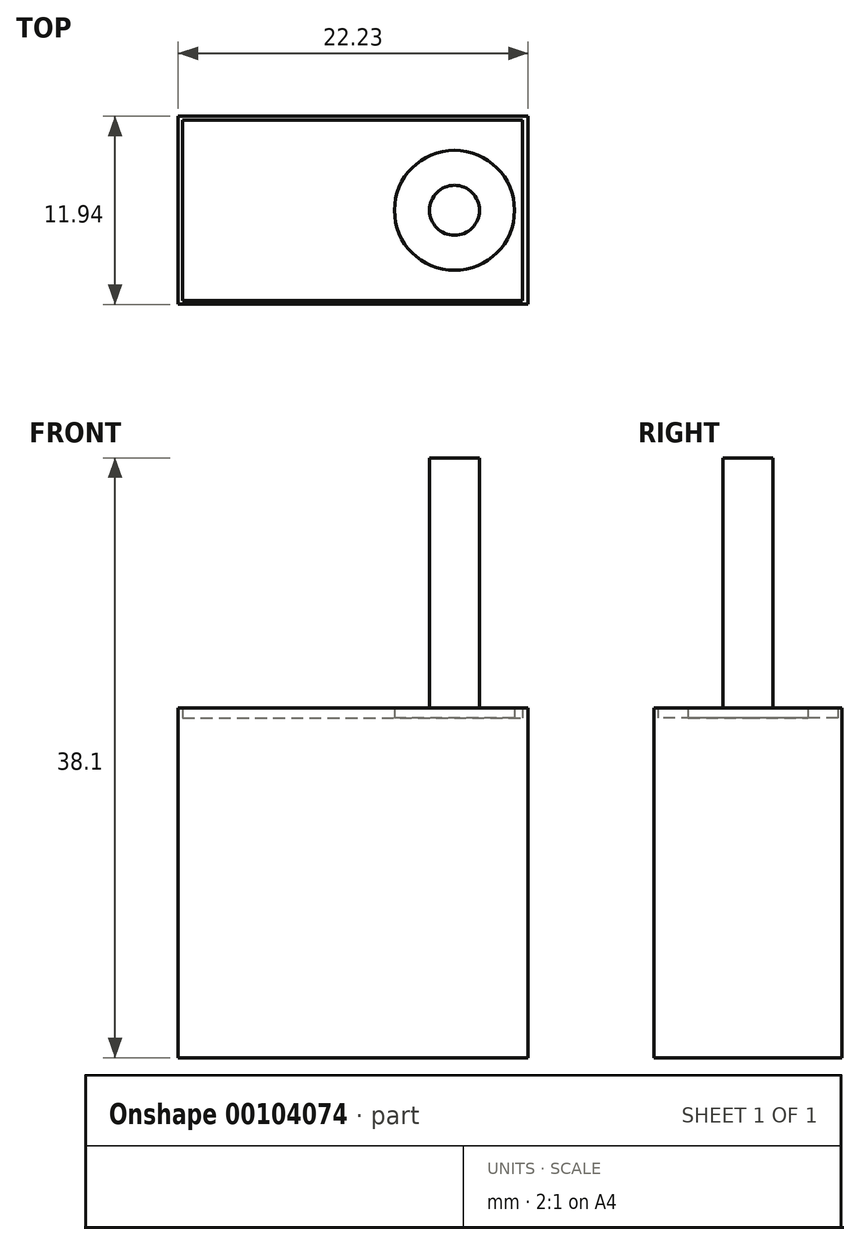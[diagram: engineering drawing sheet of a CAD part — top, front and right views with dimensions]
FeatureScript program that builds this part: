
annotation { "Feature Type Name" : "Feature", "Feature Type Description" : "" }
export const myFeature = defineFeature(function(context is Context, id is Id, definition is map)
    precondition{}
    {
        {
            var Q0;
            Q0=qCreatedBy(makeId("Top.planeOp"),FACE);
            var sketch = newSketch(context, id + "F0", { "sketchPlane" : qUnion([Q0])});
            skLineSegment(sketch, "E0.bottom", {"start": v(-55.63, 21.9) * mm, "end": v(-33.4, 21.9) * mm});
            skLineSegment(sketch, "E0.top", {"start": v(-55.63, 9.97) * mm, "end": v(-33.4, 9.97) * mm});
            skLineSegment(sketch, "E0.left", {"start": v(-55.63, 21.9) * mm, "end": v(-55.63, 9.97) * mm});
            skLineSegment(sketch, "E0.right", {"start": v(-33.4, 21.9) * mm, "end": v(-33.4, 9.97) * mm});
            skCircle(sketch, "E1", {"center": v(-38.08, 15.94) * mm, "radius": 3.81 * mm});
            skPoint(sketch, "E1.centerSnap0", {"position": v(-33.4, 15.94) * mm});
            skCircle(sketch, "E2", {"center": v(-38.08, 15.94) * mm, "radius": 1.59 * mm});
            skLineSegment(sketch, "E3.bottom", {"start": v(-55.34, 21.66) * mm, "end": v(-33.75, 21.66) * mm});
            skLineSegment(sketch, "E3.top", {"start": v(-55.34, 10.22) * mm, "end": v(-33.75, 10.22) * mm});
            skLineSegment(sketch, "E3.left", {"start": v(-55.34, 21.66) * mm, "end": v(-55.34, 10.22) * mm});
            skLineSegment(sketch, "E3.right", {"start": v(-33.75, 21.66) * mm, "end": v(-33.75, 10.22) * mm});
            skPoint(sketch, "E4", {"position": v(-44.52, 21.9) * mm});
            skPoint(sketch, "E5", {"position": v(-44.52, 15.94) * mm});
            skPoint(sketch, "E6", {"position": v(-44.52, 9.97) * mm});
            skSolve(sketch);
        }
        {
            var Q0;
            Q0=makeQuery(id+"F0.imprint","IMPRINT",FACE,{"disambiguationData":[TD([[makeQuery(id+"F0.imprint","IMPRINT",EDGE,{"derivedFrom":sQuery(id+"F0.wireOp",EDGE,"E0.bottom")}),-1.0]])]});
            extrude(context, id + "F1", {"entities" : qUnion([Q0]), "depth" : 22.22 * mm});
        }
        {
            var Q0;
            Q0=makeQuery(id+"F0.imprint","IMPRINT",FACE,{"disambiguationData":[TD([[makeQuery(id+"F0.imprint","IMPRINT",EDGE,{"derivedFrom":sQuery(id+"F0.wireOp",EDGE,"E1")}),1.0]])]});
            extrude(context, id + "F2", {"entities" : qUnion([Q0]), "operationType" : NewBodyOperationType.ADD, "depth" : 22.22 * mm});
        }
        {
            var Q0;
            Q0=makeQuery(id+"F0.imprint","IMPRINT",FACE,{"disambiguationData":[TD([[makeQuery(id+"F0.imprint","IMPRINT",EDGE,{"derivedFrom":sQuery(id+"F0.wireOp",EDGE,"E2")}),1.0]])]});
            extrude(context, id + "F3", {"entities" : qUnion([Q0]), "operationType" : NewBodyOperationType.ADD, "depth" : 38.1 * mm});
        }
        {
            var Q0;
            Q0=makeQuery(id+"F0.imprint","IMPRINT",FACE,{"disambiguationData":[TD([[makeQuery(id+"F0.imprint","IMPRINT",EDGE,{"derivedFrom":sQuery(id+"F0.wireOp",EDGE,"E1")}),-1.0]])]});
            var Q1;
            Q1=makeQuery(id+"F0.imprint","IMPRINT",FACE,{"disambiguationData":[TD([[makeQuery(id+"F0.imprint","IMPRINT",EDGE,{"derivedFrom":sQuery(id+"F0.wireOp",EDGE,"E0.bottom")}),-1.0]])]});
            extrude(context, id + "F4", {"entities" : qUnion([Q0, Q1]), "operationType" : NewBodyOperationType.ADD, "depth" : 21.59 * mm});
        }
    });
